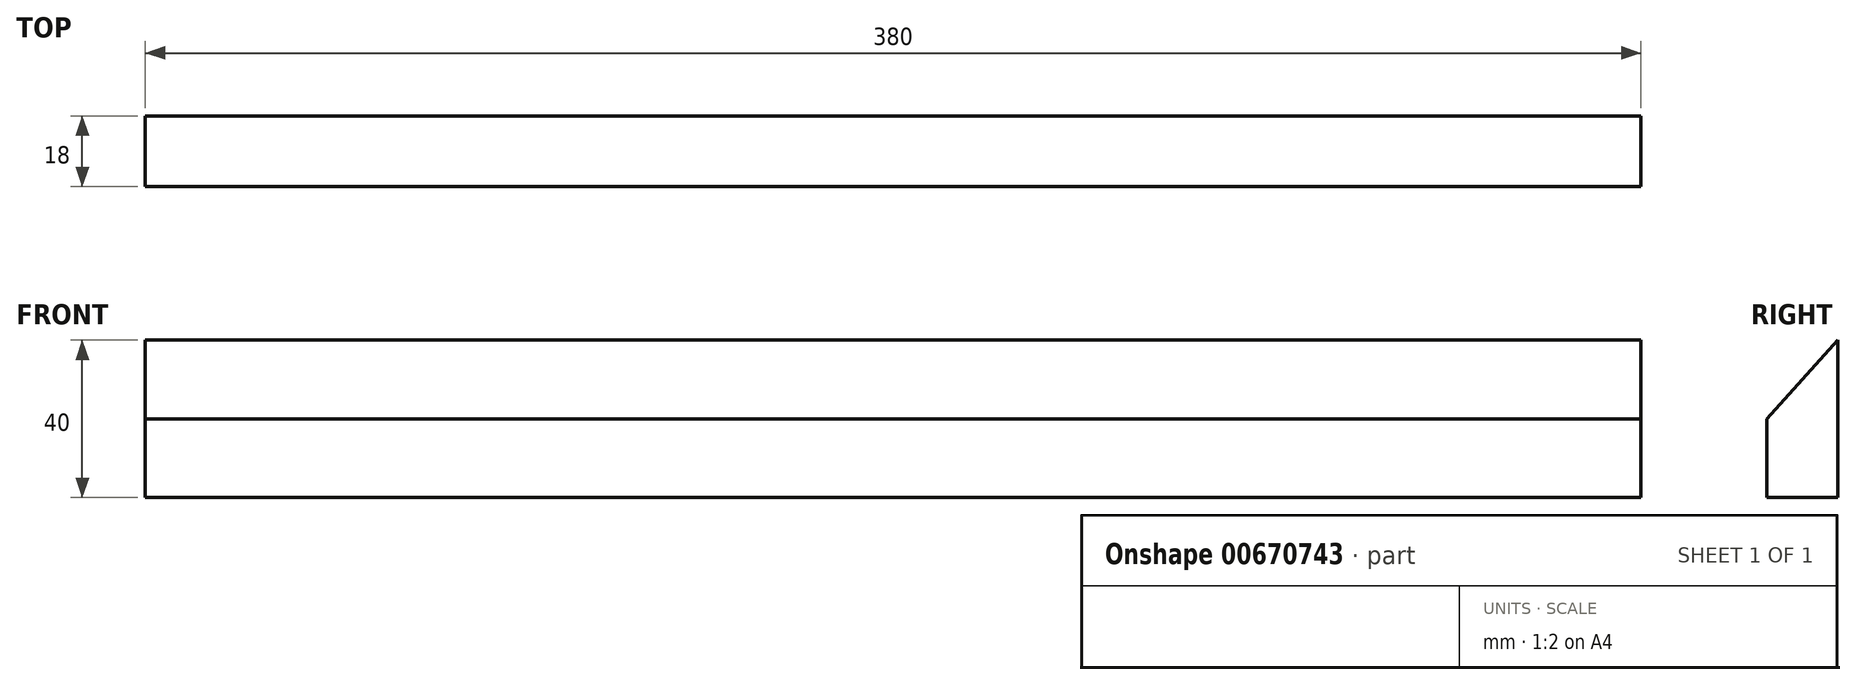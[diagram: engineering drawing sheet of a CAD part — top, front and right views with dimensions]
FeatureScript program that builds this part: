
annotation { "Feature Type Name" : "Feature", "Feature Type Description" : "" }
export const myFeature = defineFeature(function(context is Context, id is Id, definition is map)
    precondition{}
    {
        {
            var Q0;
            Q0=qCreatedBy(makeId("Right.planeOp"),FACE);
            var sketch = newSketch(context, id + "F0", { "sketchPlane" : qUnion([Q0])});
            skLineSegment(sketch, "E0", {"start": v(-9, -20) * mm, "end": v(9, -20) * mm});
            skLineSegment(sketch, "E1", {"start": v(9, -20) * mm, "end": v(9, 20) * mm});
            skLineSegment(sketch, "E2", {"start": v(9, 20) * mm, "end": v(-9, 0) * mm});
            skLineSegment(sketch, "E3", {"start": v(-9, 0) * mm, "end": v(-9, -20) * mm});
            skSolve(sketch);
        }
        {
            var Q0;
            Q0 = qSketchRegion(id + "F0", true);
            extrude(context, id + "F1", {"entities" : qUnion([Q0]), "endBound" : BoundingType.SYMMETRIC, "depth" : 380 * mm, "offsetDistance" : 25 * mm});
        }
    });
